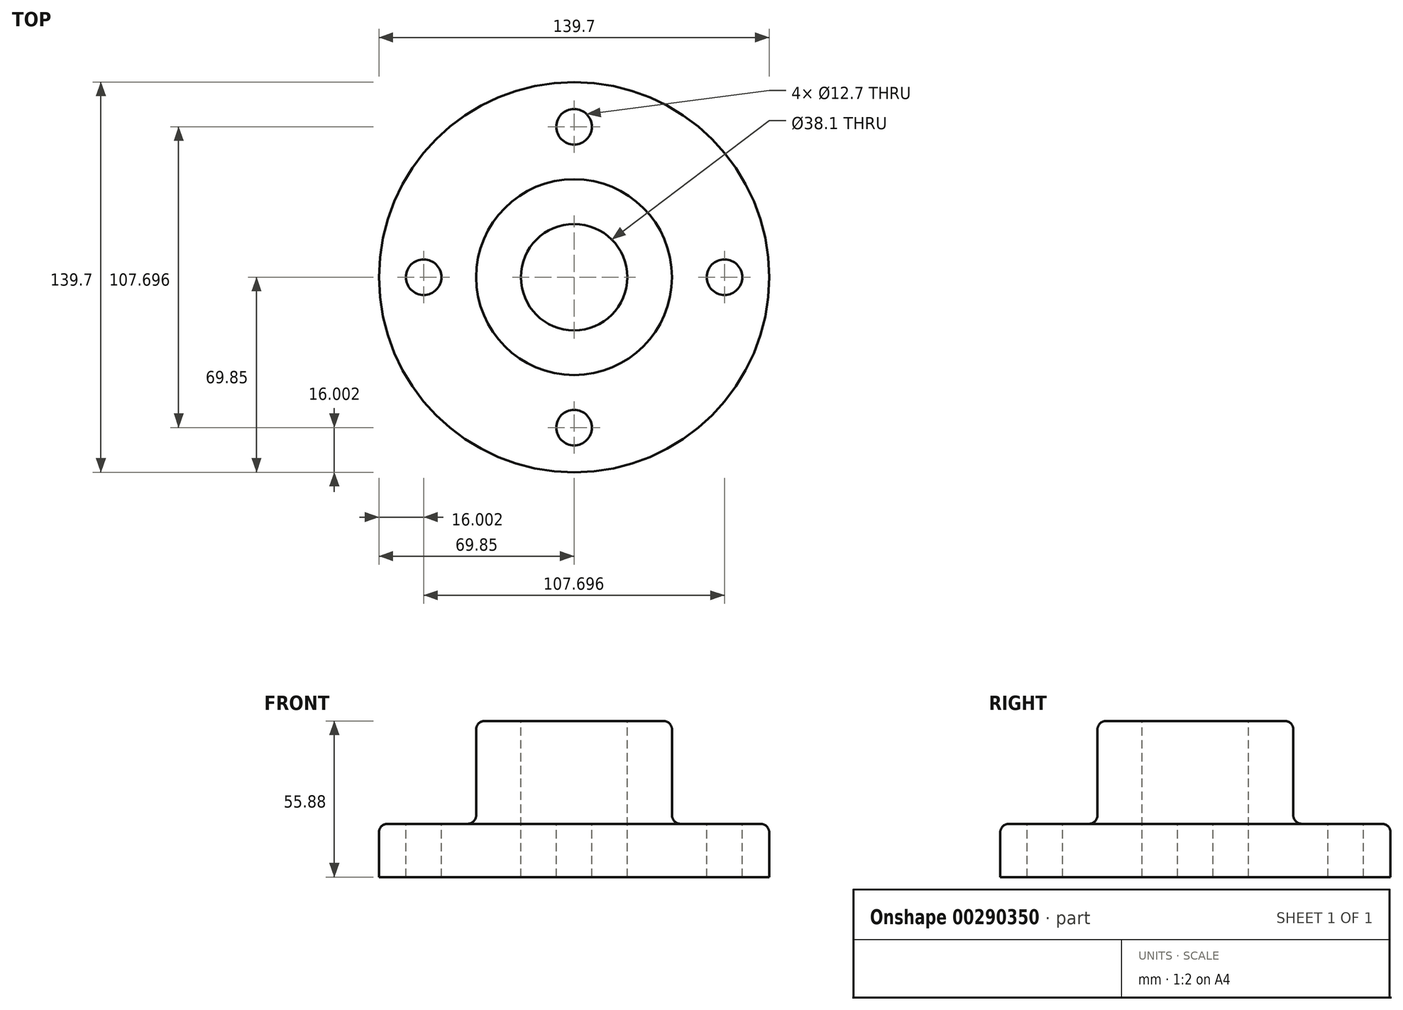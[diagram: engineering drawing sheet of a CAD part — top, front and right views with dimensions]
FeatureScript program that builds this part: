
annotation { "Feature Type Name" : "Feature", "Feature Type Description" : "" }
export const myFeature = defineFeature(function(context is Context, id is Id, definition is map)
    precondition{}
    {
        {
            var Q0;
            Q0=qCreatedBy(makeId("Front.planeOp"),FACE);
            var sketch = newSketch(context, id + "F0", { "sketchPlane" : qUnion([Q0])});
            skLineSegment(sketch, "E0", {"start": v(0, 0) * mm, "end": v(69.85, 0) * mm});
            skLineSegment(sketch, "E1", {"start": v(69.85, 0) * mm, "end": v(69.85, 19.05) * mm});
            skLineSegment(sketch, "E2", {"start": v(69.85, 19.05) * mm, "end": v(35.05, 19.05) * mm});
            skLineSegment(sketch, "E3", {"start": v(35.05, 19.05) * mm, "end": v(35.05, 55.88) * mm});
            skLineSegment(sketch, "E4", {"start": v(35.05, 55.88) * mm, "end": v(0, 55.88) * mm});
            skLineSegment(sketch, "E5", {"start": v(0, 55.88) * mm, "end": v(0, 0) * mm});
            skSolve(sketch);
        }
        {
            var Q0;
            Q0=makeQuery(id+"F0.imprint","IMPRINT",FACE,{"disambiguationData":[TD([[makeQuery(id+"F0.imprint","IMPRINT",EDGE,{"derivedFrom":sQuery(id+"F0.wireOp",EDGE,"E0")}),1.0]])]});
            var Q1;
            Q1=sQuery(id+"F0.wireOp",EDGE,"E5");
            revolve(context, id + "F1", {"entities" : qUnion([Q0]), "axis" : qUnion([Q1]), "revolveType" : RevolveType.FULL});
        }
        {
            var Q0;
            Q0=makeQuery(id+"F1.opRevolve","SWEPT_FACE",FACE,{"disambiguationData":[OSD([sQuery(id+"F0.wireOp",EDGE,"E4")])]});
            var sketch = newSketch(context, id + "F2", { "sketchPlane" : qUnion([Q0])});
            skCircle(sketch, "E6", {"center": v(0, 0) * mm, "radius": 19.05 * mm});
            skSolve(sketch);
        }
        {
            var Q0;
            Q0=makeQuery(id+"F2.imprint","IMPRINT",FACE,{"disambiguationData":[TD([[makeQuery(id+"F2.imprint","IMPRINT",EDGE,{"derivedFrom":sQuery(id+"F2.wireOp",EDGE,"E6")}),1.0]])]});
            extrude(context, id + "F3", {"entities" : qUnion([Q0]), "operationType" : NewBodyOperationType.REMOVE, "endBound" : BoundingType.THROUGH_ALL, "oppositeDirection" : true, "depth" : 25.4 * mm});
        }
        {
            var Q0;
            Q0=makeQuery(id+"F1.opRevolve","SWEPT_EDGE",EDGE,{"disambiguationData":[OSD([sQuery(id+"F0.wireOp",EDGE,"E3"),sQuery(id+"F0.wireOp",EDGE,"E4")])]});
            var Q1;
            Q1=makeQuery(id+"F1.opRevolve","SWEPT_EDGE",EDGE,{"disambiguationData":[OSD([sQuery(id+"F0.wireOp",EDGE,"E1"),sQuery(id+"F0.wireOp",EDGE,"E2")])]});
            var Q2;
            Q2=makeQuery(id+"F1.opRevolve","SWEPT_FACE",FACE,{"disambiguationData":[OSD([sQuery(id+"F0.wireOp",EDGE,"E2")])]});
            fillet(context, id + "F4", {"entities" : qUnion([Q0, Q1, Q2]), "radius" : 3.05 * mm, "tangentPropagation" : true, "allowEdgeOverflow" : false});
        }
        {
            var Q0;
            Q0=makeQuery(id+"F1.opRevolve","SWEPT_FACE",FACE,{"disambiguationData":[OSD([sQuery(id+"F0.wireOp",EDGE,"E2")])]});
            var sketch = newSketch(context, id + "F5", { "sketchPlane" : qUnion([Q0])});
            skCircle(sketch, "E7", {"center": v(-53.85, 0) * mm, "radius": 6.35 * mm});
            skCircle(sketch, "E8", {"center": v(0, 53.85) * mm, "radius": 6.35 * mm});
            skCircle(sketch, "E9", {"center": v(53.85, 0) * mm, "radius": 6.35 * mm});
            skCircle(sketch, "E10", {"center": v(0, -53.85) * mm, "radius": 6.35 * mm});
            skSolve(sketch);
        }
        {
            var Q0;
            Q0 = qSketchRegion(id + "F5", true);
            extrude(context, id + "F6", {"entities" : qUnion([Q0]), "operationType" : NewBodyOperationType.REMOVE, "endBound" : BoundingType.THROUGH_ALL, "oppositeDirection" : true, "depth" : 25.4 * mm});
        }
    });
